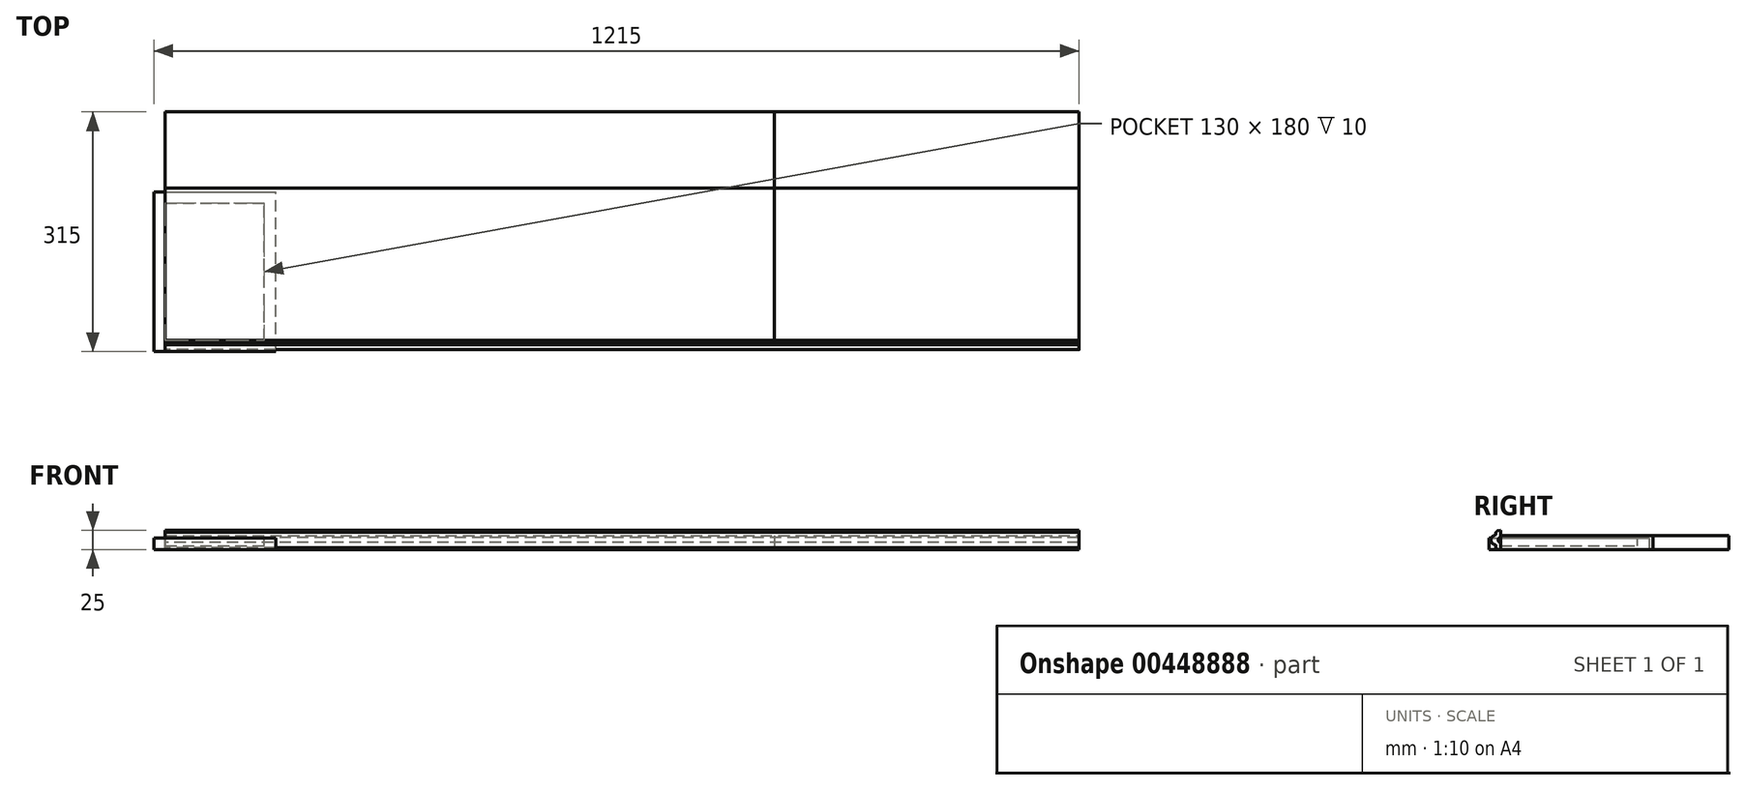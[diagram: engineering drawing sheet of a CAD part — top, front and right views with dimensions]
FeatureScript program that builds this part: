
annotation { "Feature Type Name" : "Feature", "Feature Type Description" : "" }
export const myFeature = defineFeature(function(context is Context, id is Id, definition is map)
    precondition{}
    {
        {
            var Q0;
            Q0=qCreatedBy(makeId("Top.planeOp"),FACE);
            var sketch = newSketch(context, id + "F0", { "sketchPlane" : qUnion([Q0])});
            skLineSegment(sketch, "E0.bottom", {"start": v(0, 0) * mm, "end": v(1200, 0) * mm});
            skLineSegment(sketch, "E0.top", {"start": v(0, 300) * mm, "end": v(1200, 300) * mm});
            skLineSegment(sketch, "E0.left", {"start": v(0, 0) * mm, "end": v(0, 300) * mm});
            skLineSegment(sketch, "E0.right", {"start": v(1200, 0) * mm, "end": v(1200, 300) * mm});
            skSolve(sketch);
        }
        {
            var Q0;
            Q0=makeQuery(id+"F0.imprint","IMPRINT",FACE,{"disambiguationData":[TD([[makeQuery(id+"F0.imprint","IMPRINT",EDGE,{"derivedFrom":sQuery(id+"F0.wireOp",EDGE,"E0.bottom")}),1.0]])]});
            extrude(context, id + "F1", {"entities" : qUnion([Q0]), "depth" : 18 * mm});
        }
        {
            var Q0;
            Q0=qCreatedBy(makeId("Top.planeOp"),FACE);
            var sketch = newSketch(context, id + "F2", { "sketchPlane" : qUnion([Q0])});
            skLineSegment(sketch, "E1.bottom", {"start": v(0, 0) * mm, "end": v(1200, 0) * mm});
            skLineSegment(sketch, "E1.top", {"start": v(0, 200) * mm, "end": v(1200, 200) * mm});
            skLineSegment(sketch, "E1.left", {"start": v(0, 0) * mm, "end": v(0, 200) * mm});
            skLineSegment(sketch, "E1.right", {"start": v(1200, 0) * mm, "end": v(1200, 200) * mm});
            skSolve(sketch);
        }
        {
            var Q0;
            Q0 = qSketchRegion(id + "F2", true);
            extrude(context, id + "F3", {"entities" : qUnion([Q0]), "depth" : 18 * mm});
        }
        {
            var Q0;
            Q0=qCreatedBy(makeId("Right.planeOp"),FACE);
            var sketch = newSketch(context, id + "F4", { "sketchPlane" : qUnion([Q0])});
            skLineSegment(sketch, "E2.bottom", {"start": v(0, 0) * mm, "end": v(-4.25, 0.15) * mm});
            skLineSegment(sketch, "E2.top", {"start": v(0, 25) * mm, "end": v(-4.25, 24.85) * mm});
            skLineSegment(sketch, "E2.left", {"start": v(0, 0) * mm, "end": v(0, 9.38) * mm});
            skLineSegment(sketch, "E2.right", {"start": v(-6.25, 2.22) * mm, "end": v(-6.25, 5.32) * mm});
            skArc(sketch, "E3", {"start": v(-7.1, 18.69) * mm, "mid": v(-12.5, 12.5) * mm, "end": v(-7.1, 6.31) * mm});
            skLineSegment(sketch, "E4.trimOffspring", {"start": v(-6.25, 19.68) * mm, "end": v(-6.25, 22.78) * mm});
            skLineSegment(sketch, "E5", {"start": v(-3.12, 24.9) * mm, "end": v(-3.12, 0.1) * mm, "construction": true});
            skArc(sketch, "E6", {"start": v(0, 15.62) * mm, "mid": v(-3.12, 12.5) * mm, "end": v(0, 9.38) * mm});
            skLineSegment(sketch, "E7.trimOffspring", {"start": v(0, 15.62) * mm, "end": v(0, 25) * mm});
            skPoint(sketch, "E8.visualSharp", {"position": v(-6.25, 18.75) * mm});
            skArc(sketch, "E8.filletArc", {"start": v(-7.1, 18.69) * mm, "mid": v(-6.5, 19.02) * mm, "end": v(-6.25, 19.68) * mm});
            skPoint(sketch, "E9.visualSharp", {"position": v(-6.25, 6.25) * mm});
            skArc(sketch, "E9.filletArc", {"start": v(-6.25, 5.32) * mm, "mid": v(-6.5, 5.98) * mm, "end": v(-7.1, 6.31) * mm});
            skArc(sketch, "E10", {"start": v(-4.25, 24.85) * mm, "mid": v(-4.8, 23.4) * mm, "end": v(-6.25, 22.78) * mm});
            skArc(sketch, "E11", {"start": v(-4.25, 0.15) * mm, "mid": v(-4.8, 1.6) * mm, "end": v(-6.25, 2.22) * mm});
            skSolve(sketch);
        }
        {
            var Q0;
            Q0 = qSketchRegion(id + "F4", true);
            extrude(context, id + "F5", {"entities" : qUnion([Q0]), "depth" : 1200 * mm});
        }
        {
            var Q0;
            Q0=qCreatedBy(makeId("Top.planeOp"),FACE);
            var sketch = newSketch(context, id + "F6", { "sketchPlane" : qUnion([Q0])});
            skLineSegment(sketch, "E12.bottom", {"start": v(0, 0) * mm, "end": v(800, 0) * mm});
            skLineSegment(sketch, "E12.top", {"start": v(0, 300) * mm, "end": v(800, 300) * mm});
            skLineSegment(sketch, "E12.left", {"start": v(0, 0) * mm, "end": v(0, 300) * mm});
            skLineSegment(sketch, "E12.right", {"start": v(800, 0) * mm, "end": v(800, 300) * mm});
            skSolve(sketch);
        }
        {
            var Q0;
            Q0 = qSketchRegion(id + "F6", true);
            extrude(context, id + "F7", {"entities" : qUnion([Q0]), "depth" : 18 * mm});
        }
        {
            var Q0;
            Q0=qCreatedBy(makeId("Top.planeOp"),FACE);
            var sketch = newSketch(context, id + "F8", { "sketchPlane" : qUnion([Q0])});
            skLineSegment(sketch, "E13.bottom", {"start": v(0, 0) * mm, "end": v(130, 0) * mm, "construction": true});
            skLineSegment(sketch, "E13.top", {"start": v(0, 180) * mm, "end": v(130, 180) * mm, "construction": true});
            skLineSegment(sketch, "E13.left", {"start": v(0, 0) * mm, "end": v(0, 180) * mm, "construction": true});
            skLineSegment(sketch, "E13.right", {"start": v(130, 0) * mm, "end": v(130, 180) * mm, "construction": true});
            skLineSegment(sketch, "E14.0", {"start": v(-15, 195) * mm, "end": v(145, 195) * mm});
            skLineSegment(sketch, "E14.1", {"start": v(-15, -15) * mm, "end": v(-15, 195) * mm});
            skLineSegment(sketch, "E14.2", {"start": v(-15, -15) * mm, "end": v(145, -15) * mm});
            skLineSegment(sketch, "E14.3", {"start": v(145, -15) * mm, "end": v(145, 195) * mm});
            skSolve(sketch);
        }
        {
            var Q0;
            Q0 = qSketchRegion(id + "F8", true);
            extrude(context, id + "F9", {"entities" : qUnion([Q0]), "depth" : 15 * mm});
        }
        {
            var Q0;
            Q0=makeQuery(id+"F9.opExtrude","CAP_FACE",FACE,{"disambiguationData":[OSD([sQuery(id+"F8.wireOp",EDGE,"E14.0"),sQuery(id+"F8.wireOp",EDGE,"E14.1"),sQuery(id+"F8.wireOp",EDGE,"E14.2"),sQuery(id+"F8.wireOp",EDGE,"E14.3")])],"isStart":false});
            var sketch = newSketch(context, id + "F10", { "sketchPlane" : qUnion([Q0])});
            skLineSegment(sketch, "E15.0", {"start": v(0, 180) * mm, "end": v(130, 180) * mm});
            skLineSegment(sketch, "E16.0", {"start": v(130, 0) * mm, "end": v(130, 180) * mm});
            skLineSegment(sketch, "E17.0", {"start": v(0, 0) * mm, "end": v(130, 0) * mm});
            skLineSegment(sketch, "E18.0", {"start": v(0, 0) * mm, "end": v(0, 180) * mm});
            skSolve(sketch);
        }
        {
            var Q0;
            Q0 = qSketchRegion(id + "F10", true);
            extrude(context, id + "F11", {"entities" : qUnion([Q0]), "operationType" : NewBodyOperationType.REMOVE, "oppositeDirection" : true, "depth" : 10 * mm});
        }
    });
